# Revit family: Mount_RigidRail_Kattsafe_MetalDeck
name_source: partatom
category: Specialty Equipment
units: mm (PartAtom-declared; Revit-internal decimal feet)

## family parameters
Always vertical = Yes
Cut with Voids When Loaded = No
Enable Cutting in Views = No
Maintain Annotation Orientation = No
OmniClass Number = 23.27.71.21
Part Type = Normal
Room Calculation Point = No
Round Connector Dimension = Use Diameter
Shared = No
Work Plane-Based = No

## types (2) — shared parameters
Assembly Code = E1090100
Description = Rigid rails provide significant spanning capabilities, making them very versatile where there are limited support structures. The high strength aluminium construction, along with the unique t-bolt assembly makes it a very simple and easily adaptable system to install.
Export Type to IFC As = IfcBuildingElementProxy
IfcExportAs = IfcBuildingElementProxy
IfcExportType = USERDEFINED
Manufacturer = Kattsafe®
ManufacturerOverallDepth = 269 mm  [stored 0.882546 ft]
ManufacturerOverallWidth = 552 mm  [stored 1.81102 ft]
ManufacturerSpecCode = OH253
ManufacturerURLProductSpecific = https://kattsafe.com.au
Material = Steel_Stainless_Kattsafe_Satin
Model = OH253
ModifiedIssue = 20240430 $
Type IFC Predefined Type = USERDEFINED
URL = https://kattsafe.com.au
Uniclass2015Code = Pr_20_85_09
Uniclass2015Title = Brackets
Uniclass2015Version = Products v1.23
zero-valued in all types: Default Elevation

## per-type parameters (varying)
| type | HorizontalRailBracket | ManufacturerOverallHeight | Type Comments | VerticalRailBracket |
| Horizontal Rail | Yes | 100 mm  [stored 0.328084 ft] | Deck Mount Bracket - Horizontal Rail | No |
| Vertical Rail | No | 134 mm | Deck Mount Bracket - Vertical Rail | Yes |

note: [stored X ft] marks values corroborated as IEEE doubles in the binary element streams (Revit-internal decimal feet)

## geometry (parser evidence)
native form markers: Sweep x5
no freeform markers — native parametric forms only
